FCSTD DOCUMENT  (FreeCAD 0.20R29177 +426 (Git))
Label: ExtensionCalc
License: All rights reserved
LicenseURL: http://en.wikipedia.org/wiki/All_rights_reserved
objects: App::DocumentObjectGroup×3, Sketcher::SketchObject×1, PartDesign::Body×1, PartDesign::CoordinateSystem×1, App::FeaturePython×1, App::Part×1
note: 3 computed .brp shape members not serialized (recipe doc carries the construction recipe); baked Part::Feature solids carry a one-line shape summary decoded from their .brp
EXTERNAL_REF file=Params.FCStd obj=Spreadsheet

FEATURE [App::DocumentObjectGroup] Parts
FEATURE [Sketcher::SketchObject] Sketch  label="ExtensionCalc"
  FullyConstrained = true
  MapMode = 5
  Support = -> [XY_Plane001]
  expr: Constraints[1] = <<Variables>>.Rotation
  expr: Constraints[24] = <<Variables>>.MaxArmRadius
  expr: Constraints[27] = <<Variables>>.ActiveWidth
  expr: Constraints[28] = <<Variables>>.ActiveLength
  expr: Constraints[29] = <<Variables>>.ArmLength
  expr: Constraints[40] = <<Variables>>.WallMargin
  expr: Constraints[41] = <<Variables>>.WallMargin
  sketch-geometry (17):
    g0: LineSegment StartX=0 StartY=0 StartZ=0 EndX=1.087e-13 EndY=1775 EndZ=0
    g1: GeomPoint X=0 Y=0 Z=0
    g2: ArcOfCircle CenterX=0 CenterY=0 CenterZ=0 NormalX=0 NormalY=0 NormalZ=1 AngleXU=0 Radius=2120 StartAngle=2.14933 EndAngle=2.56306
    g3: LineSegment StartX=-1159.21 StartY=1775 StartZ=0 EndX=1159.21 EndY=1775 EndZ=0
    g4: ArcOfCircle CenterX=0 CenterY=0 CenterZ=0 NormalX=0 NormalY=0 NormalZ=1 AngleXU=0 Radius=2120 StartAngle=0.578536 EndAngle=0.99226
    g5: LineSegment StartX=1775 StartY=1159.21 StartZ=0 EndX=1775 EndY=-1159.21 EndZ=0
    g6: ArcOfCircle CenterX=0 CenterY=0 CenterZ=0 NormalX=0 NormalY=0 NormalZ=1 AngleXU=0 Radius=2120 StartAngle=5.29092 EndAngle=5.70465
    g7: LineSegment StartX=1159.21 StartY=-1775 StartZ=0 EndX=-1159.21 EndY=-1775 EndZ=0
    g8: ArcOfCircle CenterX=0 CenterY=0 CenterZ=0 NormalX=0 NormalY=0 NormalZ=1 AngleXU=0 Radius=2120 StartAngle=3.72013 EndAngle=4.13385
    g9: LineSegment StartX=-1775 StartY=-1159.21 StartZ=0 EndX=-1775 EndY=1159.21 EndZ=0
    g10: GeomPoint X=-1775 Y=1775 Z=0
    g11: GeomPoint X=1775 Y=-1775 Z=0
    g12: LineSegment StartX=-1825 StartY=-1825 StartZ=0 EndX=-1825 EndY=1825 EndZ=0
    g13: LineSegment StartX=-1825 StartY=1825 StartZ=0 EndX=1825 EndY=1825 EndZ=0
    g14: LineSegment StartX=1825 StartY=1825 StartZ=0 EndX=1825 EndY=-1825 EndZ=0
    g15: LineSegment StartX=1825 StartY=-1825 StartZ=0 EndX=-1825 EndY=-1825 EndZ=0
    g16: GeomPoint X=0 Y=0 Z=0
  constraints (42):
    c: Coincident(g0,g-1)
    c: Angle(g-2,g0) = 0
    c: Coincident(g1,g0)
    c: Horizontal(g3)
    c: Horizontal(g7)
    c: Vertical(g5)
    c: Vertical(g9)
    c: Equal(g2,g4)
    c: PointOnObject(g10,g3)
    c: PointOnObject(g10,g9)
    c: PointOnObject(g11,g5)
    c: PointOnObject(g11,g7)
    c: Coincident(g6,g0)
    c: Coincident(g6,g5)
    c: Coincident(g6,g7)
    c: Coincident(g8,g7)
    c: Coincident(g9,g8)
    c: Coincident(g9,g2)
    c: Coincident(g3,g2)
    c: Coincident(g3,g4)
    c: Coincident(g4,g5)
    c: Coincident(g4,g0)
    c: Coincident(g8,g0)
    c: Coincident(g2,g0)
    c: Radius(g4) = 2120
    c: Symmetric(g8,g4,g0)
    c: Symmetric(g6,g2,g0)
    c: DistanceY(g6,g3) = 3550
    c: DistanceX(g8,g5) = 3550
    c: Distance(g0) = 1775
    c: Coincident(g12,g13)
    c: Coincident(g13,g14)
    c: Coincident(g14,g15)
    c: Coincident(g15,g12)
    c: Horizontal(g13)
    c: Horizontal(g15)
    c: Vertical(g12)
    c: Vertical(g14)
    c: Symmetric(g13,g12,g16)
    c: Coincident(g16,g0)
    c: DistanceY(g3,g13) = 50
    c: DistanceX(g12,g2) = 50
FEATURE [PartDesign::Body] Body
  Group = -> [Sketch]
  Origin = -> Origin001
FEATURE [PartDesign::CoordinateSystem] LCS_Origin
  AttacherType = Attacher::AttachEngine3D
  MapMode = 2
  Support = -> [X_Axis]
FEATURE [App::FeaturePython] Variables  # WARN: FeaturePython — macro-defined, semantics opaque (R4)
  ActiveLength = 3550
  ActiveWidth = 3550
  ArmCos = 2120
  ArmLength = 1775
  ArmSin = 0
  MaxArmRadius = 2120
  Retraction = 345
  RoomLength = 3650
  RoomWidth = 3650
  Rotation = 0
  Type = App::PropertyContainer
  WallMargin = 50
  expr: ActiveLength = RoomLength - WallMargin * 2
  expr: ActiveWidth = RoomWidth - WallMargin * 2
  expr: ArmCos = cos(Rotation) * MaxArmRadius
  expr: ArmLength = abs(ArmCos) > ActiveWidth / 2 ? ActiveWidth / 2 / abs(ArmCos) * MaxArmRadius : (abs(ArmSin) > ActiveLength / 2 ? ActiveLength / 2 / abs(ArmSin) * MaxArmRadius : MaxArmRadius)
  expr: ArmSin = sin(Rotation) * MaxArmRadius
  expr: Retraction = MaxArmRadius - ArmLength
  expr: RoomLength = <<Params>>#<<Params>>.RoomLength
  expr: RoomWidth = <<Params>>#<<Params>>.RoomWidth
FEATURE [App::DocumentObjectGroup] Constraints
FEATURE [App::DocumentObjectGroup] Configurations
FEATURE [App::Part] Assembly
  AssemblyType = Part::Link
  Group = -> [LCS_Origin,Variables,Constraints,Configurations]
  Origin = -> Origin
  Type = Assembly
